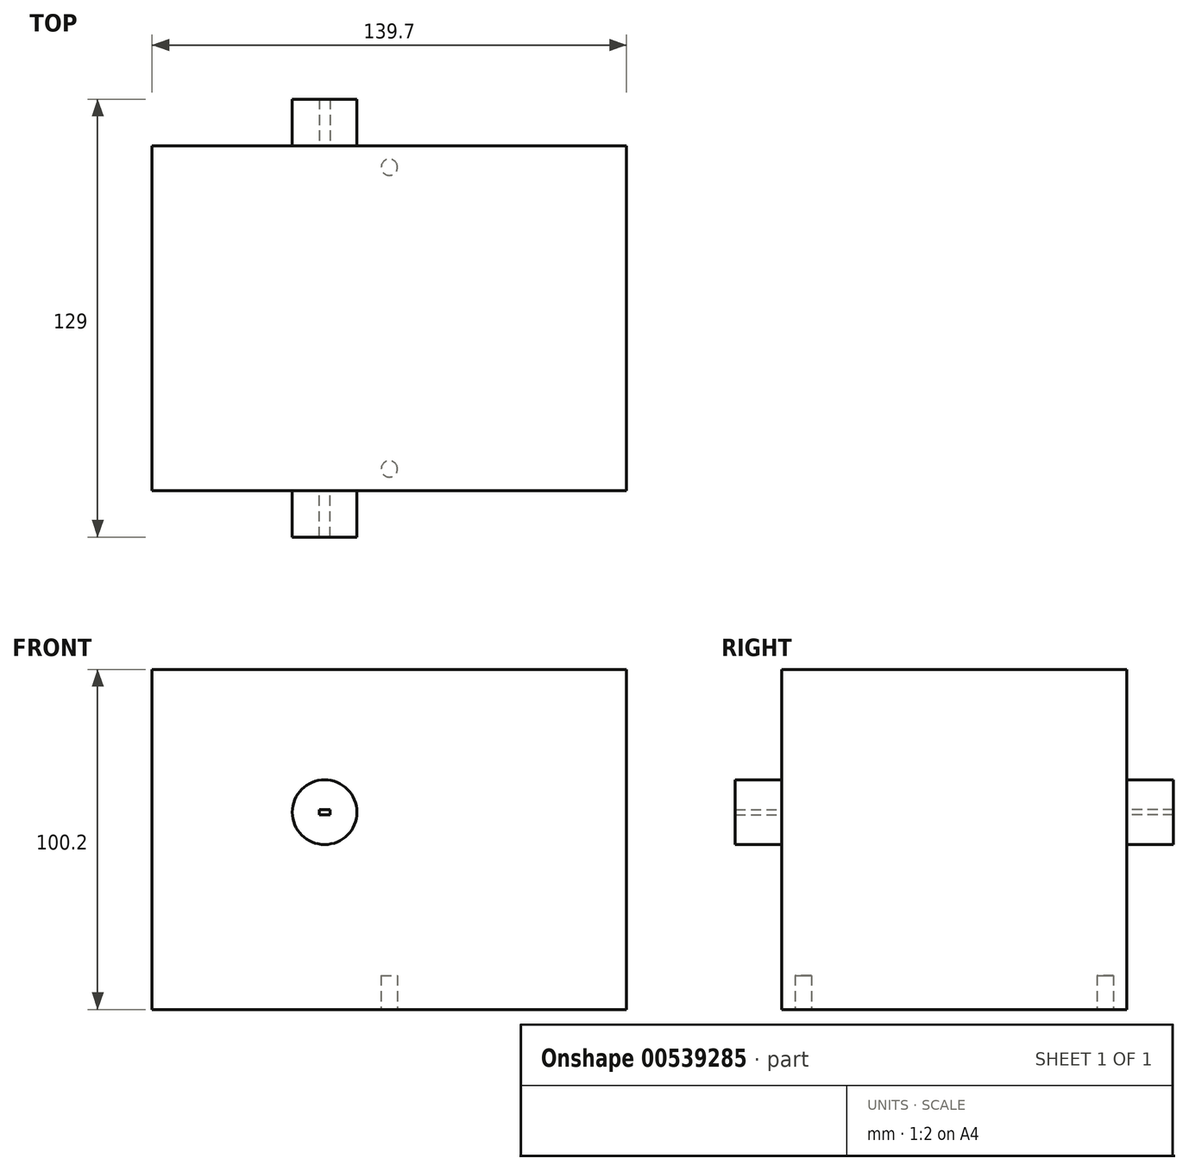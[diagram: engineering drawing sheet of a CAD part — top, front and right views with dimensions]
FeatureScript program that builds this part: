
annotation { "Feature Type Name" : "Feature", "Feature Type Description" : "" }
export const myFeature = defineFeature(function(context is Context, id is Id, definition is map)
    precondition{}
    {
        {
            var Q0;
            Q0=qCreatedBy(makeId("Front.planeOp"),FACE);
            var sketch = newSketch(context, id + "F0", { "sketchPlane" : qUnion([Q0])});
            skLineSegment(sketch, "E0", {"start": v(-50.8, 42.08) * mm, "end": v(-50.8, -58.12) * mm});
            skLineSegment(sketch, "E1", {"start": v(-50.8, -58.12) * mm, "end": v(88.9, -58.12) * mm});
            skLineSegment(sketch, "E2", {"start": v(-50.8, 42.08) * mm, "end": v(88.9, 42.08) * mm});
            skLineSegment(sketch, "E3", {"start": v(88.9, 42.08) * mm, "end": v(88.9, -58.12) * mm});
            skLineSegment(sketch, "E4.bottom", {"start": v(-1.55, -0.78) * mm, "end": v(1.55, -0.78) * mm});
            skLineSegment(sketch, "E4.top", {"start": v(-1.55, 0.77) * mm, "end": v(1.55, 0.77) * mm});
            skLineSegment(sketch, "E4.left", {"start": v(-1.55, -0.78) * mm, "end": v(-1.55, 0.77) * mm});
            skLineSegment(sketch, "E4.right", {"start": v(1.55, -0.78) * mm, "end": v(1.55, 0.77) * mm});
            skPoint(sketch, "E4.middle", {"position": v(0, 0) * mm});
            skCircle(sketch, "E5", {"center": v(0, 0) * mm, "radius": 9.53 * mm});
            skSolve(sketch);
        }
        {
            var Q0;
            Q0=makeQuery(id+"F0.imprint","IMPRINT",FACE,{"disambiguationData":[TD([[makeQuery(id+"F0.imprint","IMPRINT",EDGE,{"derivedFrom":sQuery(id+"F0.wireOp",EDGE,"E4.bottom")}),-1.0]])]});
            var Q1;
            Q1=makeQuery(id+"F0.imprint","IMPRINT",FACE,{"disambiguationData":[TD([[makeQuery(id+"F0.imprint","IMPRINT",EDGE,{"derivedFrom":sQuery(id+"F0.wireOp",EDGE,"E4.bottom")}),1.0]])]});
            var Q2;
            Q2=makeQuery(id+"F0.imprint","IMPRINT",FACE,{"disambiguationData":[TD([[makeQuery(id+"F0.imprint","IMPRINT",EDGE,{"derivedFrom":sQuery(id+"F0.wireOp",EDGE,"E0")}),1.0]])]});
            extrude(context, id + "F1", {"entities" : qUnion([Q0, Q1, Q2]), "depth" : 101.6 * mm, "offsetDistance" : 25 * mm});
        }
        {
            var Q0;
            Q0=makeQuery(id+"F0.imprint","IMPRINT",FACE,{"disambiguationData":[TD([[makeQuery(id+"F0.imprint","IMPRINT",EDGE,{"derivedFrom":sQuery(id+"F0.wireOp",EDGE,"E4.bottom")}),-1.0]])]});
            extrude(context, id + "F2", {"entities" : qUnion([Q0]), "operationType" : NewBodyOperationType.ADD, "oppositeDirection" : true, "depth" : 13.7 * mm, "offsetDistance" : 25 * mm});
        }
        {
            var Q0;
            Q0=qCreatedBy(makeId("Front.planeOp"),FACE);
            cPlane(context, id + "F3", {"entities" : qUnion([Q0]), "cplaneType" : CPlaneType.OFFSET, "offset" : 101.6 * mm, "width" : 150 * mm, "height" : 150 * mm});
        }
        {
            var Q0;
            Q0=qCreatedBy(id+"F3.planeOp",FACE);
            var sketch = newSketch(context, id + "F4", { "sketchPlane" : qUnion([Q0])});
            skLineSegment(sketch, "E6.bottom", {"start": v(-1.55, -0.78) * mm, "end": v(1.55, -0.78) * mm});
            skLineSegment(sketch, "E6.top", {"start": v(-1.55, 0.78) * mm, "end": v(1.55, 0.78) * mm});
            skLineSegment(sketch, "E6.left", {"start": v(-1.55, -0.78) * mm, "end": v(-1.55, 0.78) * mm});
            skLineSegment(sketch, "E6.right", {"start": v(1.55, -0.78) * mm, "end": v(1.55, 0.78) * mm});
            skPoint(sketch, "E6.middle", {"position": v(0, 0) * mm});
            skCircle(sketch, "E7", {"center": v(0, 0) * mm, "radius": 9.53 * mm});
            skSolve(sketch);
        }
        {
            var Q0;
            Q0=makeQuery(id+"F4.imprint","IMPRINT",FACE,{"disambiguationData":[TD([[makeQuery(id+"F4.imprint","IMPRINT",EDGE,{"derivedFrom":sQuery(id+"F4.wireOp",EDGE,"E6.bottom")}),-1.0]])]});
            extrude(context, id + "F5", {"entities" : qUnion([Q0]), "operationType" : NewBodyOperationType.ADD, "depth" : 13.7 * mm, "offsetDistance" : 25 * mm});
        }
        {
            var Q0;
            Q0=makeQuery(id+"F1.opExtrude","SWEPT_FACE",FACE,{"disambiguationData":[OSD([sQuery(id+"F0.wireOp",EDGE,"E1")])]});
            var sketch = newSketch(context, id + "F6", { "sketchPlane" : qUnion([Q0])});
            skLineSegment(sketch, "E8", {"start": v(-50.8, 50.8) * mm, "end": v(19.05, 50.8) * mm});
            skLineSegment(sketch, "E9", {"start": v(19.05, 50.8) * mm, "end": v(19.05, 6.35) * mm});
            skLineSegment(sketch, "E10", {"start": v(19.05, 50.8) * mm, "end": v(19.05, 95.25) * mm});
            skCircle(sketch, "E11", {"center": v(19.05, 6.35) * mm, "radius": 2.4 * mm});
            skCircle(sketch, "E12", {"center": v(19.05, 95.25) * mm, "radius": 2.4 * mm});
            skSolve(sketch);
        }
        {
            var Q0;
            Q0=makeQuery(id+"F6.imprint","IMPRINT",FACE,{"disambiguationData":[TD([[makeQuery(id+"F6.imprint","IMPRINT",EDGE,{"derivedFrom":sQuery(id+"F6.wireOp",EDGE,"E12")}),1.0]])]});
            var Q1;
            Q1=makeQuery(id+"F6.imprint","IMPRINT",FACE,{"disambiguationData":[TD([[makeQuery(id+"F6.imprint","IMPRINT",EDGE,{"derivedFrom":sQuery(id+"F6.wireOp",EDGE,"E11")}),1.0]])]});
            extrude(context, id + "F7", {"entities" : qUnion([Q0, Q1]), "operationType" : NewBodyOperationType.REMOVE, "oppositeDirection" : true, "depth" : 10 * mm, "offsetDistance" : 25 * mm});
        }
    });
